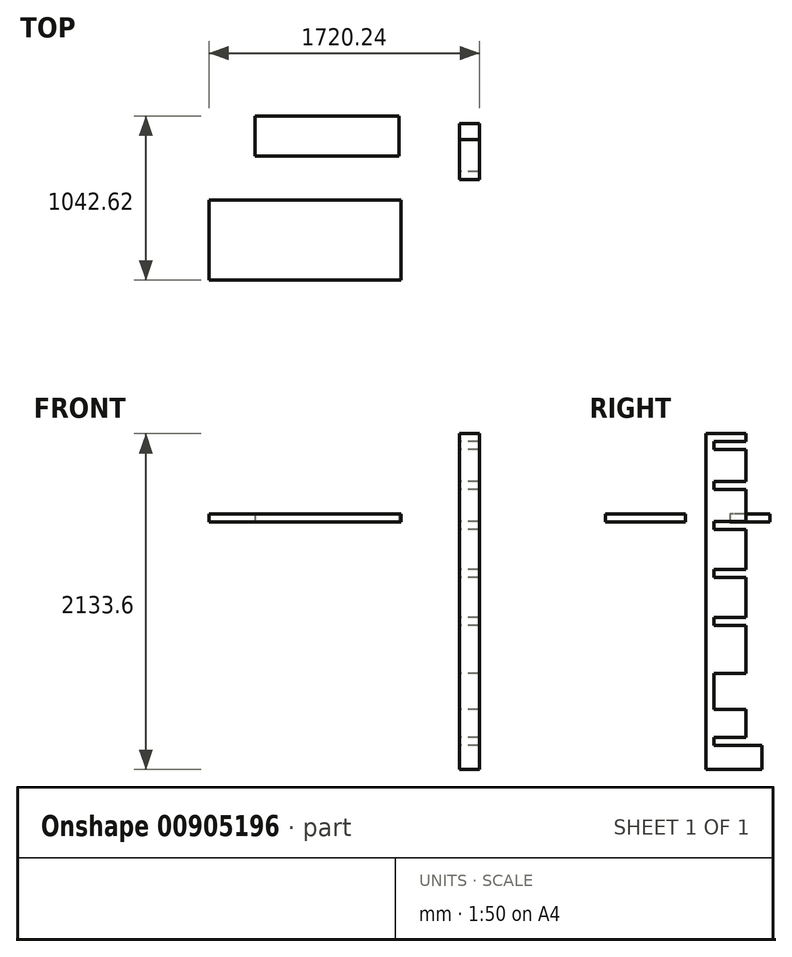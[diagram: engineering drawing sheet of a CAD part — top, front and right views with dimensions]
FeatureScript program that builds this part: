
annotation { "Feature Type Name" : "Feature", "Feature Type Description" : "" }
export const myFeature = defineFeature(function(context is Context, id is Id, definition is map)
    precondition{}
    {
        {
            var Q0;
            Q0=qCreatedBy(makeId("Right.planeOp"),FACE);
            var sketch = newSketch(context, id + "F0", { "sketchPlane" : qUnion([Q0])});
            skLineSegment(sketch, "E0", {"start": v(-138.5, 562.39) * mm, "end": v(-138.5, -1571.21) * mm});
            skLineSegment(sketch, "E1", {"start": v(-138.5, -1571.21) * mm, "end": v(217.1, -1571.21) * mm});
            skLineSegment(sketch, "E2", {"start": v(217.1, -1571.21) * mm, "end": v(217.1, -1418.81) * mm});
            skLineSegment(sketch, "E3", {"start": v(217.1, -1418.81) * mm, "end": v(-87.7, -1418.81) * mm});
            skLineSegment(sketch, "E4", {"start": v(-87.7, -1418.81) * mm, "end": v(-87.7, -1368.01) * mm});
            skLineSegment(sketch, "E5", {"start": v(-87.7, -1368.01) * mm, "end": v(115.5, -1368.01) * mm});
            skLineSegment(sketch, "E6", {"start": v(115.5, -1368.01) * mm, "end": v(115.5, -1188.36) * mm});
            skLineSegment(sketch, "E7", {"start": v(115.5, -1188.36) * mm, "end": v(-87.7, -1188.36) * mm});
            skLineSegment(sketch, "E8", {"start": v(-87.7, -1188.36) * mm, "end": v(-87.7, -961.61) * mm});
            skLineSegment(sketch, "E9", {"start": v(-87.7, -961.61) * mm, "end": v(115.5, -961.61) * mm});
            skLineSegment(sketch, "E10", {"start": v(115.5, -47.21) * mm, "end": v(-87.7, -47.21) * mm});
            skLineSegment(sketch, "E11", {"start": v(-87.7, -47.21) * mm, "end": v(115.5, -47.21) * mm});
            skLineSegment(sketch, "E12", {"start": v(-87.7, 3.59) * mm, "end": v(-87.7, -47.21) * mm});
            skLineSegment(sketch, "E13", {"start": v(115.5, 3.59) * mm, "end": v(-87.7, 3.59) * mm});
            skLineSegment(sketch, "E14", {"start": v(115.5, 3.59) * mm, "end": v(115.5, 206.79) * mm});
            skLineSegment(sketch, "E15", {"start": v(115.5, 206.79) * mm, "end": v(-87.7, 206.79) * mm});
            skLineSegment(sketch, "E16", {"start": v(-87.7, 206.79) * mm, "end": v(-87.7, 257.59) * mm});
            skLineSegment(sketch, "E17", {"start": v(-87.7, 257.59) * mm, "end": v(115.5, 257.59) * mm});
            skLineSegment(sketch, "E18", {"start": v(115.5, 257.59) * mm, "end": v(115.5, 460.79) * mm});
            skLineSegment(sketch, "E19", {"start": v(115.5, 460.79) * mm, "end": v(-87.7, 460.79) * mm});
            skLineSegment(sketch, "E20", {"start": v(-87.7, 460.79) * mm, "end": v(-87.7, 511.59) * mm});
            skLineSegment(sketch, "E21", {"start": v(-87.7, 511.59) * mm, "end": v(115.5, 511.59) * mm});
            skLineSegment(sketch, "E22", {"start": v(115.5, 511.59) * mm, "end": v(115.5, 562.39) * mm});
            skPoint(sketch, "E23.start.orphan", {"position": v(-14.36, 562.39) * mm});
            skPoint(sketch, "E24.end.orphan", {"position": v(-87.7, -606.01) * mm});
            skPoint(sketch, "E25.orphan", {"position": v(-138.5, 562.39) * mm});
            skLineSegment(sketch, "E26", {"start": v(-138.5, 562.39) * mm, "end": v(115.5, 562.39) * mm});
            skLineSegment(sketch, "E27", {"start": v(115.5, -47.21) * mm, "end": v(115.5, -301.21) * mm});
            skLineSegment(sketch, "E28", {"start": v(115.5, -301.21) * mm, "end": v(-87.7, -301.21) * mm});
            skLineSegment(sketch, "E29", {"start": v(-87.7, -301.21) * mm, "end": v(-87.7, -352.01) * mm});
            skLineSegment(sketch, "E30", {"start": v(-87.7, -352.01) * mm, "end": v(115.5, -352.01) * mm});
            skLineSegment(sketch, "E31", {"start": v(115.5, -352.01) * mm, "end": v(115.5, -606.01) * mm});
            skLineSegment(sketch, "E32", {"start": v(115.5, -606.01) * mm, "end": v(-87.7, -606.01) * mm});
            skLineSegment(sketch, "E33", {"start": v(-87.7, -656.81) * mm, "end": v(-87.7, -606.01) * mm});
            skLineSegment(sketch, "E34", {"start": v(-87.7, -656.81) * mm, "end": v(115.5, -656.81) * mm});
            skLineSegment(sketch, "E35", {"start": v(115.5, -656.81) * mm, "end": v(115.5, -961.61) * mm});
            skSolve(sketch);
        }
        {
            var Q0;
            Q0=makeQuery(id+"F0.imprint","IMPRINT",FACE,{"disambiguationData":[TD([[makeQuery(id+"F0.imprint","IMPRINT",EDGE,{"derivedFrom":sQuery(id+"F0.wireOp",EDGE,"E0")}),1.0]])]});
            extrude(context, id + "F1", {"entities" : qUnion([Q0]), "endBound" : BoundingType.SYMMETRIC, "depth" : 127 * mm, "offsetDistance" : 25.4 * mm});
        }
        {
            var Q0;
            Q0=qCreatedBy(makeId("Top.planeOp"),FACE);
            var sketch = newSketch(context, id + "F2", { "sketchPlane" : qUnion([Q0])});
            skLineSegment(sketch, "E36.bottom", {"start": v(-448.99, 266.29) * mm, "end": v(-1363.39, 266.29) * mm});
            skLineSegment(sketch, "E36.top", {"start": v(-448.99, 12.29) * mm, "end": v(-1363.39, 12.29) * mm});
            skLineSegment(sketch, "E36.left", {"start": v(-448.99, 266.29) * mm, "end": v(-448.99, 12.29) * mm});
            skLineSegment(sketch, "E36.right", {"start": v(-1363.39, 266.29) * mm, "end": v(-1363.39, 12.29) * mm});
            skSolve(sketch);
        }
        {
            var Q0;
            Q0=makeQuery(id+"F2.imprint","IMPRINT",FACE,{"disambiguationData":[TD([[makeQuery(id+"F2.imprint","IMPRINT",EDGE,{"derivedFrom":sQuery(id+"F2.wireOp",EDGE,"E36.bottom")}),1.0]])]});
            extrude(context, id + "F3", {"entities" : qUnion([Q0]), "depth" : 50.8 * mm, "offsetDistance" : 25.4 * mm});
        }
        {
            var Q0;
            Q0=qCreatedBy(makeId("Top.planeOp"),FACE);
            var sketch = newSketch(context, id + "F4", { "sketchPlane" : qUnion([Q0])});
            skLineSegment(sketch, "E37.bottom", {"start": v(-1656.74, -268.33) * mm, "end": v(-437.54, -268.33) * mm});
            skLineSegment(sketch, "E37.top", {"start": v(-1656.74, -776.33) * mm, "end": v(-437.54, -776.33) * mm});
            skLineSegment(sketch, "E37.left", {"start": v(-1656.74, -268.33) * mm, "end": v(-1656.74, -776.33) * mm});
            skLineSegment(sketch, "E37.right", {"start": v(-437.54, -268.33) * mm, "end": v(-437.54, -776.33) * mm});
            skSolve(sketch);
        }
        {
            var Q0;
            Q0 = qSketchRegion(id + "F4", true);
            extrude(context, id + "F5", {"entities" : qUnion([Q0]), "depth" : 50.8 * mm, "offsetDistance" : 25.4 * mm});
        }
    });
